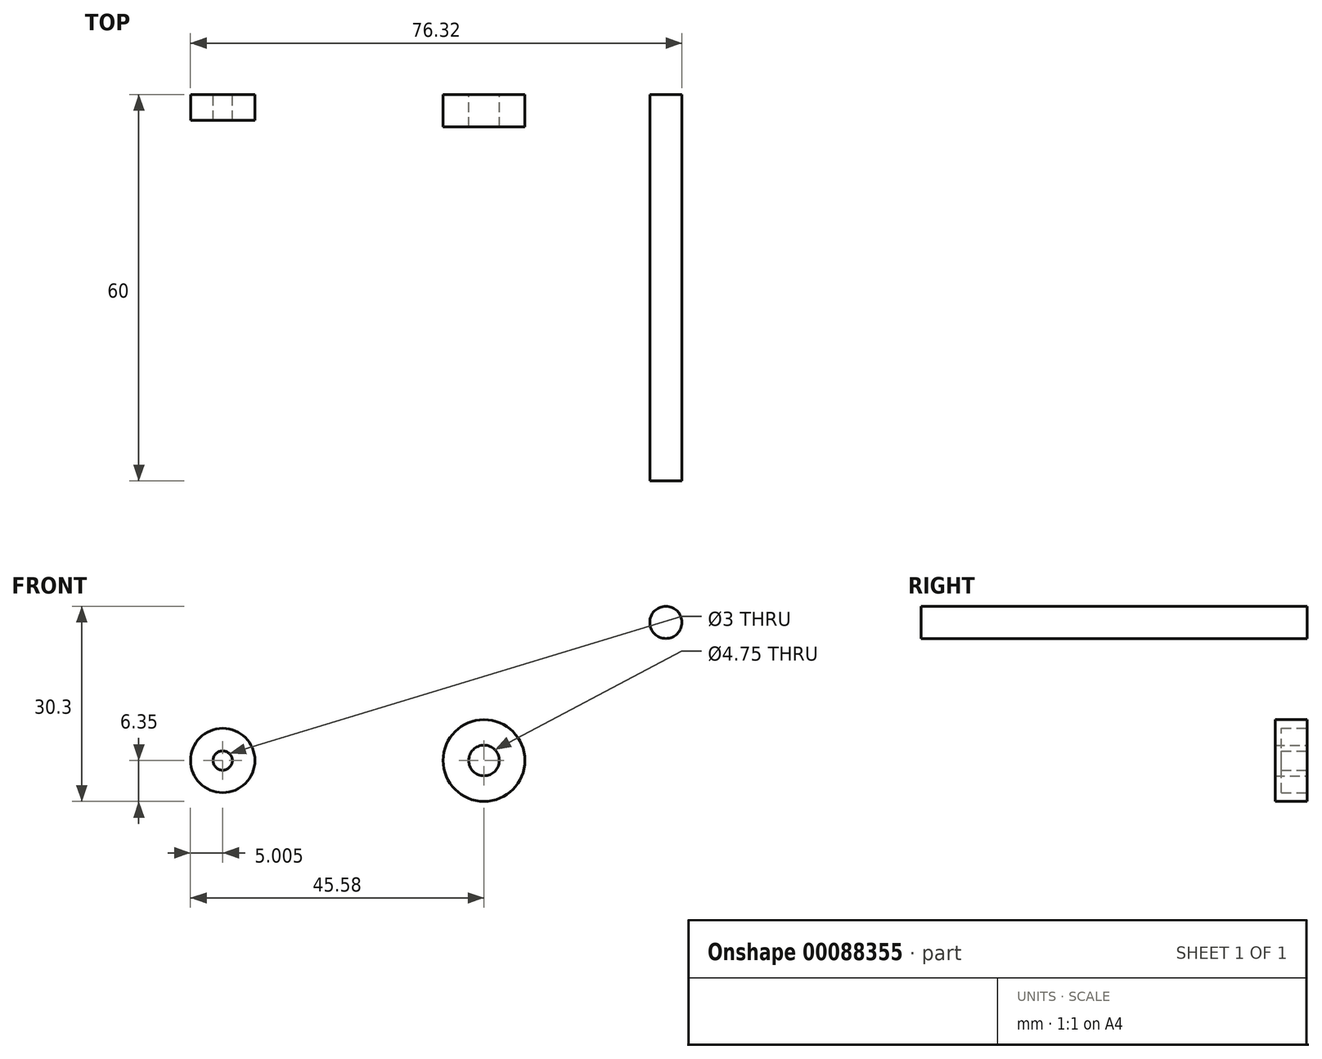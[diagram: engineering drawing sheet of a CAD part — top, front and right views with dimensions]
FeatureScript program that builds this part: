
annotation { "Feature Type Name" : "Feature", "Feature Type Description" : "" }
export const myFeature = defineFeature(function(context is Context, id is Id, definition is map)
    precondition{}
    {
        {
            var Q0;
            Q0=qCreatedBy(makeId("Front.planeOp"),FACE);
            var sketch = newSketch(context, id + "F0", { "sketchPlane" : qUnion([Q0])});
            skCircle(sketch, "E0", {"center": v(0, 0) * mm, "radius": 2.38 * mm});
            skCircle(sketch, "E1", {"center": v(0, 0) * mm, "radius": 6.35 * mm});
            skSolve(sketch);
        }
        {
            var Q0;
            Q0 = qSketchRegion(id + "F0", true);
            extrude(context, id + "F1", {"entities" : qUnion([Q0]), "depth" : 5 * mm});
        }
        {
            var Q0;
            Q0=qCreatedBy(makeId("Front.planeOp"),FACE);
            var sketch = newSketch(context, id + "F2", { "sketchPlane" : qUnion([Q0])});
            skCircle(sketch, "E2", {"center": v(28.24, 21.45) * mm, "radius": 2.5 * mm});
            skSolve(sketch);
        }
        {
            var Q0;
            Q0 = qSketchRegion(id + "F2", true);
            extrude(context, id + "F3", {"entities" : qUnion([Q0]), "depth" : 60 * mm});
        }
        {
            var Q0;
            Q0=qCreatedBy(makeId("Front.planeOp"),FACE);
            var sketch = newSketch(context, id + "F4", { "sketchPlane" : qUnion([Q0])});
            skCircle(sketch, "E3", {"center": v(-40.58, 0) * mm, "radius": 1.5 * mm});
            skCircle(sketch, "E4", {"center": v(-40.58, 0) * mm, "radius": 5 * mm});
            skSolve(sketch);
        }
        {
            var Q0;
            Q0 = qSketchRegion(id + "F4", true);
            extrude(context, id + "F5", {"entities" : qUnion([Q0]), "depth" : 4 * mm});
        }
    });
